# Revit family: HCL_Latchways_FallArrestSystemGuidedAnchorLine_90degreeCornerSet
name_source: partatom
category: Generic Models
revit_build: Autodesk Revit 2014 (Build: 20130308_1515(x64)
units: mm (PartAtom-declared; Revit-internal decimal feet)

## types (1)
- ManSafe CFP - 90 degree Corner Set
    AssetType = Fixed
    AttachmentDeviceGuide = https://www.latchways.com
    BIMObjectName = HCL_Latchways_FallArrestSystemGuidedAnchorLine_90degreeCornerSet
    Default Elevation = 1219 mm
    Description = Latchways ManSafe® for Roofing, using Constant Force posts
    DurationUnit = year
    FireExit = No
    IfcExportAs = NOTDEFINED
    IfcExportType = IfcTransportElement
    Installer Website = https://www.hclsafety.com
    ManSafeForRoofingBrochure = https://www.hclsafety.com
    ManufacturerName = MSA Latchways
    ManufacturerURL = www.latchways.com
    Model = 65012-00
    ModelNumber = 65012-00
    ModelReference = Constant Force Post  - 90 degree Corner Set
    NBSDescription = Fall arrest system - guided anchor line
    NBSReference = 80-50-25/110
    Name = FallArrestSystemGuidedAnchorLine_90degreeCornerSet_MSA_Latchways
    NominalHeight = 43 mm
    NominalLength = 480 mm  [stored 1.5748 ft]
    NominalWidth = 480 mm  [stored 1.5748 ft]
    PreInstallationSurvey = Required
    ProductInformation = www.latchways.com/BIM/65012-00_ExtendedOnePieceCornerBracket.pdf
    ProductSpecification = www.latchways.com/BIM/Latchways_Specification_ConstantForcePost.pdf
    Size = 480 x 480 x 42.5 mm
    SystemMaintenance = Annual service to be completed by HCL Safety in accordance with BS7883:2005
    SystemManufacturer = MSA Latchways
    URL = www.latchways.com
    Uniclass2 = 80-30-25/135
    Version = 1
    WarrantyDurationUnit = year

note: [stored X ft] marks values corroborated as IEEE doubles in the binary element streams (Revit-internal decimal feet)

## geometry (parser evidence)
native form markers: Sweep x3
no freeform markers — native parametric forms only
